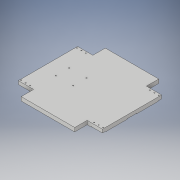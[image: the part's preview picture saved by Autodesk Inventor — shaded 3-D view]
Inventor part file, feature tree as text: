
AUTODESK INVENTOR PART (.ipt)
format: ipt  version: 2017 (Build 210142000, 142)  size: 195,584 bytes
history: native  units: in
note: dims shown in document units (in); Inventor stores cm internally (conversion verified against a paired STEP export)
features: extrude x2, sketch x2
ambient origin geometry x8: Origin, YZ Plane, XZ Plane, XY Plane, X Axis, Y Axis, Z Axis, Center Point
bodies: Solid1 (feature_tree)
feature tree (4):
  extrude  "Extrusion1"  Depth=0.0625in TaperAngle=0.0deg
  extrude  "Extrusion2"  [1 undecoded]
  sketch  "Sketch1"  dims[d1=0.7874in d3=0.7874in d4=11.0in d5=11.0in d6=2.0in d7=1.625in d8=2.0in d9=1.625in d10=2.0in d11=1.625in d12=1.625in d13=5.0in d14=1.25in d15=1.5in d16=0.5in d17=0.125in d18=7.299in d19=9.551in d20=0.5in d21=0.0in]
  sketch  "Sketch3"  dims[d23=0.7874in d25=0.7874in d26=11.0in d27=11.0in d30=2.0in d31=1.625in d32=2.0in d33=1.625in d34=1.625in d35=5.0in d36=1.25in d37=1.5in d38=0.5in d39=0.125in d40=7.299in d41=9.551in d42=0.0625in d43=0.0in]
note: 1 required parameter value undecoded (feature->parameter linkage not recoverable at this tier; creation-order binding heuristic only, values carry confidence <= 0.55)
